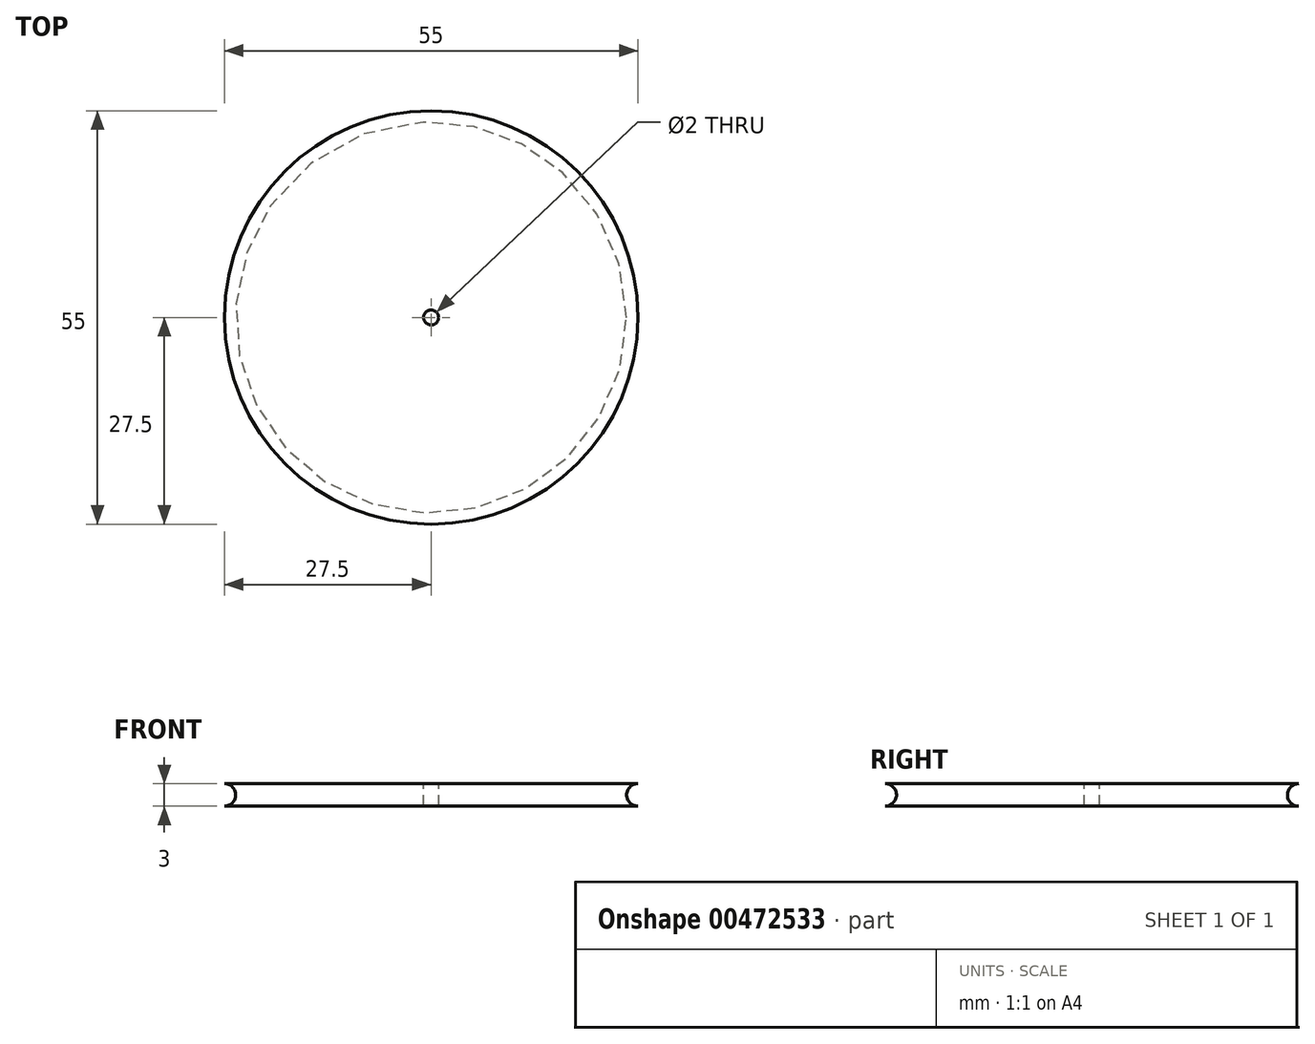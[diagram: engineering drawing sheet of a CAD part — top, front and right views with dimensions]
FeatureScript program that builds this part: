
annotation { "Feature Type Name" : "Feature", "Feature Type Description" : "" }
export const myFeature = defineFeature(function(context is Context, id is Id, definition is map)
    precondition{}
    {
        {
            var Q0;
            Q0=qCreatedBy(makeId("Front.planeOp"),FACE);
            var sketch = newSketch(context, id + "F0", { "sketchPlane" : qUnion([Q0])});
            skLineSegment(sketch, "E0", {"start": v(0, 27.28) * mm, "end": v(0, -34.94) * mm, "construction": true});
            skLineSegment(sketch, "E1", {"start": v(0, 0) * mm, "end": v(27.5, 0) * mm});
            skLineSegment(sketch, "E2", {"start": v(0, 3) * mm, "end": v(27.5, 3) * mm});
            skLineSegment(sketch, "E3", {"start": v(0, 0) * mm, "end": v(0, 3) * mm});
            skLineSegment(sketch, "E4", {"start": v(27.5, 3) * mm, "end": v(27.5, 0) * mm, "construction": true});
            skArc(sketch, "E5", {"start": v(27.5, 3) * mm, "mid": v(26, 1.5) * mm, "end": v(27.5, 0) * mm});
            skSolve(sketch);
        }
        {
            var Q0;
            Q0=makeQuery(id+"F0.imprint","IMPRINT",FACE,{"disambiguationData":[TD([[makeQuery(id+"F0.imprint","IMPRINT",EDGE,{"derivedFrom":sQuery(id+"F0.wireOp",EDGE,"E1")}),1.0]])]});
            var Q1;
            Q1=sQuery(id+"F0.wireOp",EDGE,"E0");
            revolve(context, id + "F1", {"entities" : qUnion([Q0]), "axis" : qUnion([Q1]), "revolveType" : RevolveType.FULL});
        }
        {
            var Q0;
            Q0=makeQuery(id+"F1.opRevolve","SWEPT_FACE",FACE,{"disambiguationData":[OSD([sQuery(id+"F0.wireOp",EDGE,"E2")])]});
            var sketch = newSketch(context, id + "F2", { "sketchPlane" : qUnion([Q0])});
            skCircle(sketch, "E6", {"center": v(0, 0) * mm, "radius": 1 * mm});
            skSolve(sketch);
        }
        {
            var Q0;
            Q0=makeQuery(id+"F2.imprint","IMPRINT",FACE,{"disambiguationData":[TD([[makeQuery(id+"F2.imprint","IMPRINT",EDGE,{"derivedFrom":sQuery(id+"F2.wireOp",EDGE,"E6")}),1.0]])]});
            extrude(context, id + "F3", {"entities" : qUnion([Q0]), "operationType" : NewBodyOperationType.REMOVE, "oppositeDirection" : true, "depth" : 3 * mm});
        }
    });
